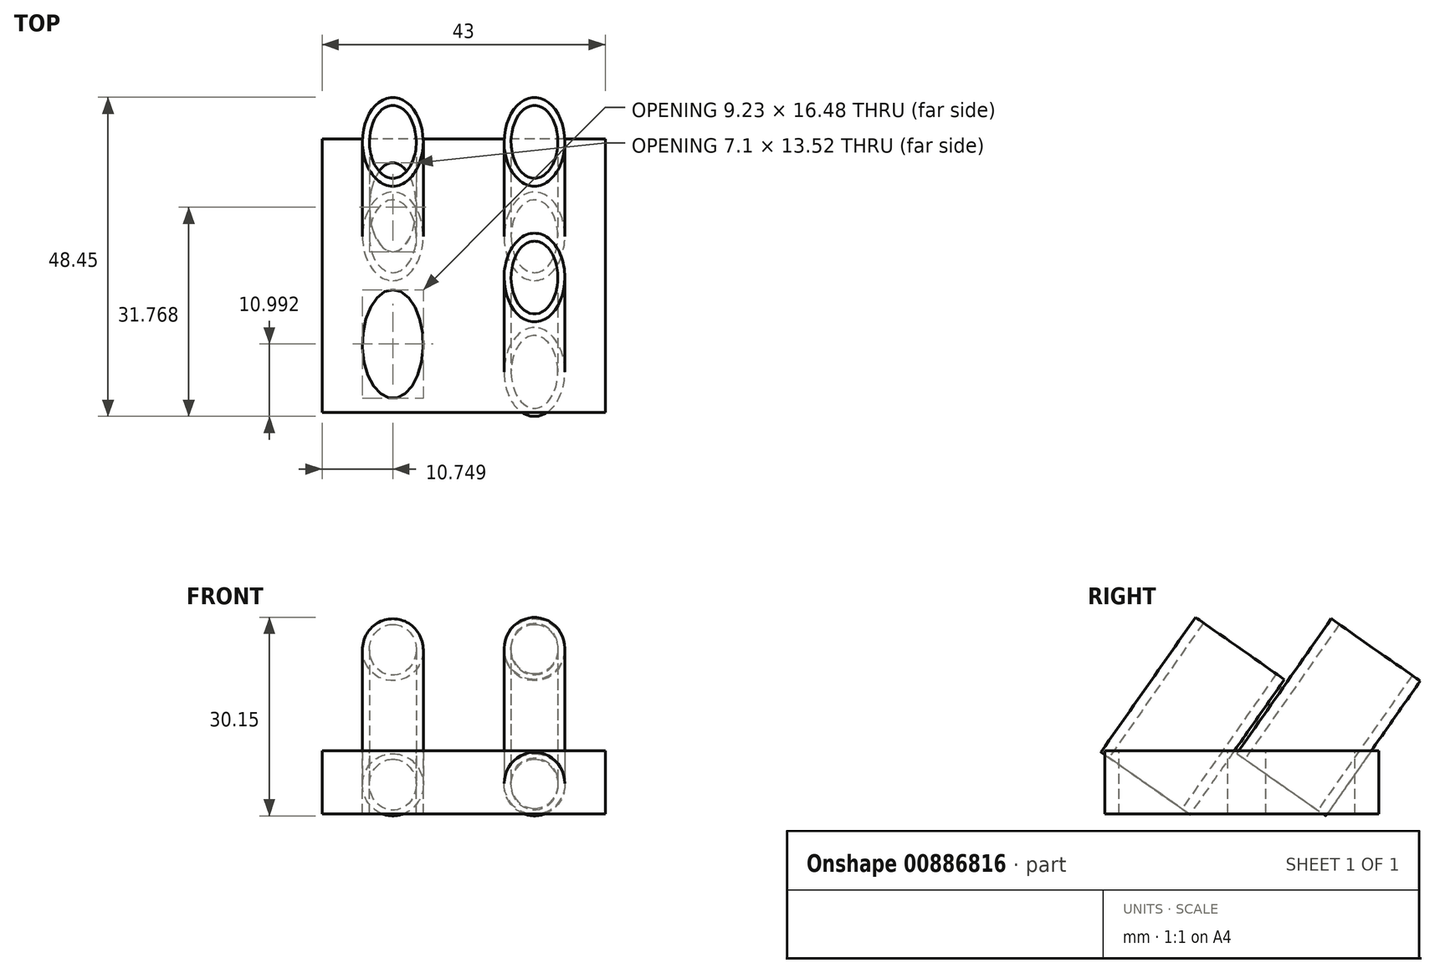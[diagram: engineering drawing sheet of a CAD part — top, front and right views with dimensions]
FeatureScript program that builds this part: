
annotation { "Feature Type Name" : "Feature", "Feature Type Description" : "" }
export const myFeature = defineFeature(function(context is Context, id is Id, definition is map)
    precondition{}
    {
        {
            var Q0;
            Q0=qCreatedBy(makeId("Top.planeOp"),FACE);
            var sketch = newSketch(context, id + "F0", { "sketchPlane" : qUnion([Q0])});
            skLineSegment(sketch, "E0.bottom", {"start": v(21.5, 20.78) * mm, "end": v(-21.5, 20.78) * mm});
            skLineSegment(sketch, "E0.top", {"start": v(21.5, -20.78) * mm, "end": v(-21.5, -20.78) * mm});
            skLineSegment(sketch, "E0.left", {"start": v(21.5, 20.78) * mm, "end": v(21.5, -20.78) * mm});
            skLineSegment(sketch, "E0.right", {"start": v(-21.5, 20.78) * mm, "end": v(-21.5, -20.78) * mm});
            skPoint(sketch, "E0.middle", {"position": v(0, 0) * mm});
            skEllipse(sketch, "E1", {"center": v(-10.75, -10.39) * mm, "majorRadius": 6.76 * mm, "minorRadius": 3.55 * mm, "majorAxis": v(0, 1)});
            skEllipse(sketch, "E2.MirrorC", {"center": v(-10.75, -10.39) * mm, "majorRadius": 6.76 * mm, "minorRadius": 3.55 * mm, "majorAxis": v(0, 1)});
            skEllipse(sketch, "E3.MirrorC", {"center": v(-10.75, -10.39) * mm, "majorRadius": 6.76 * mm, "minorRadius": 3.55 * mm, "majorAxis": v(0, 1)});
            skEllipse(sketch, "E4", {"center": v(-10.75, -10.39) * mm, "majorRadius": 8.24 * mm, "minorRadius": 4.62 * mm, "majorAxis": v(0, 1)});
            skEllipse(sketch, "E5.MirrorC", {"center": v(-10.75, 10.39) * mm, "majorRadius": 8.24 * mm, "minorRadius": 4.62 * mm, "majorAxis": v(0, -1)});
            skEllipse(sketch, "E6.MirrorC", {"center": v(-10.75, 10.39) * mm, "majorRadius": 6.76 * mm, "minorRadius": 3.55 * mm, "majorAxis": v(0, -1)});
            skEllipse(sketch, "E7.MirrorC", {"center": v(-10.75, 10.39) * mm, "majorRadius": 6.76 * mm, "minorRadius": 3.55 * mm, "majorAxis": v(0, -1)});
            skEllipse(sketch, "E8.MirrorC", {"center": v(10.75, -10.39) * mm, "majorRadius": 8.24 * mm, "minorRadius": 4.62 * mm, "majorAxis": v(0, 1)});
            skEllipse(sketch, "E9.MirrorC", {"center": v(10.75, -10.39) * mm, "majorRadius": 6.76 * mm, "minorRadius": 3.55 * mm, "majorAxis": v(0, 1)});
            skEllipse(sketch, "E10.MirrorC", {"center": v(10.75, 10.39) * mm, "majorRadius": 6.76 * mm, "minorRadius": 3.55 * mm, "majorAxis": v(0, -1)});
            skEllipse(sketch, "E11.MirrorC", {"center": v(10.75, 10.39) * mm, "majorRadius": 8.24 * mm, "minorRadius": 4.62 * mm, "majorAxis": v(0, -1)});
            skLineSegment(sketch, "E12", {"start": v(-21.5, 0) * mm, "end": v(21.5, 0) * mm});
            skSolve(sketch);
        }
        {
            var Q0;
            Q0=makeQuery(id+"F0.imprint","IMPRINT",FACE,{"disambiguationData":[TD([[makeQuery(id+"F0.imprint","IMPRINT",EDGE,{"derivedFrom":sQuery(id+"F0.wireOp",EDGE,"E5.MirrorC")}),1.0]])]});
            var Q1;
            Q1=makeQuery(id+"F0.imprint","IMPRINT",FACE,{"disambiguationData":[TD([[makeQuery(id+"F0.imprint","IMPRINT",EDGE,{"derivedFrom":sQuery(id+"F0.wireOp",EDGE,"E10.MirrorC")}),-1.0]])]});
            var Q2;
            Q2=makeQuery(id+"F0.imprint","IMPRINT",FACE,{"disambiguationData":[TD([[makeQuery(id+"F0.imprint","IMPRINT",EDGE,{"derivedFrom":sQuery(id+"F0.wireOp",EDGE,"E8.MirrorC")}),1.0]])]});
            var Q3;
            Q3=makeQuery(id+"F0.imprint","IMPRINT",FACE,{"disambiguationData":[TD([[makeQuery(id+"F0.imprint","IMPRINT",EDGE,{"derivedFrom":sQuery(id+"F0.wireOp",EDGE,"E3.MirrorC")}),-1.0]])]});
            extrude(context, id + "F1", {"entities" : qUnion([Q0, Q1, Q2, Q3]), "depth" : 25 * mm, "offsetDistance" : 25 * mm});
        }
        {
            var Q0;
            Q0=sQuery(id+"F0.wireOp",EDGE,"E12");
            extrude(context, id + "F2", {"bodyType" : ToolBodyType.SURFACE, "surfaceEntities" : qUnion([Q0]), "depth" : 4.4 * mm, "offsetDistance" : 25 * mm});
        }
        {
            var Q0;
            Q0=makeQuery(id+"F1.opExtrude","SWEPT_BODY",BODY,{"disambiguationData":[OSD([sQuery(id+"F0.wireOp",EDGE,"E5.MirrorC"),sQuery(id+"F0.wireOp",EDGE,"E7.MirrorC")])]});
            var Q1;
            Q1=makeQuery(id+"F1.opExtrude","SWEPT_BODY",BODY,{"disambiguationData":[OSD([sQuery(id+"F0.wireOp",EDGE,"E10.MirrorC"),sQuery(id+"F0.wireOp",EDGE,"E11.MirrorC")])]});
            var Q2;
            Q2=makeQuery(id+"F1.opExtrude","SWEPT_BODY",BODY,{"disambiguationData":[OSD([sQuery(id+"F0.wireOp",EDGE,"E3.MirrorC"),sQuery(id+"F0.wireOp",EDGE,"E4")])]});
            var Q3;
            Q3=makeQuery(id+"F1.opExtrude","SWEPT_BODY",BODY,{"disambiguationData":[OSD([sQuery(id+"F0.wireOp",EDGE,"E8.MirrorC"),sQuery(id+"F0.wireOp",EDGE,"E9.MirrorC")])]});
            var Q4;
            Q4=makeQuery(id+"F2.opExtrude","CAP_EDGE",EDGE,{"disambiguationData":[OSD([sQuery(id+"F0.wireOp",EDGE,"E12")])],"isStart":false});
            transform(context, id + "F3", {"entities" : qUnion([Q0, Q1, Q2, Q3]), "transformType" : TransformType.ROTATION, "transformAxis" : qUnion([Q4]), "angle" : 35 * degree, "oppositeDirection" : true, "makeCopy" : false});
        }
        {
            var Q0;
            {var subQ1=sQuery(id+"F0.wireOp",EDGE,"E0.bottom");Q0=makeQuery(id+"F0.imprint","IMPRINT",FACE,{"disambiguationData":[TD([[makeQuery(id+"F0.imprint","IMPRINT",EDGE,{"derivedFrom":subQ1}),1.0]])]});}
            var Q1;
            {var subQ1=sQuery(id+"F0.wireOp",EDGE,"E0.top");Q1=makeQuery(id+"F0.imprint","IMPRINT",FACE,{"disambiguationData":[TD([[makeQuery(id+"F0.imprint","IMPRINT",EDGE,{"derivedFrom":subQ1}),-1.0]])]});}
            var Q2;
            Q2=makeQuery(id+"F0.imprint","IMPRINT",FACE,{"disambiguationData":[TD([[makeQuery(id+"F0.imprint","IMPRINT",EDGE,{"derivedFrom":sQuery(id+"F0.wireOp",EDGE,"E3.MirrorC")}),1.0]])]});
            var Q3;
            Q3=makeQuery(id+"F0.imprint","IMPRINT",FACE,{"disambiguationData":[TD([[makeQuery(id+"F0.imprint","IMPRINT",EDGE,{"derivedFrom":sQuery(id+"F0.wireOp",EDGE,"E3.MirrorC")}),-1.0]])]});
            var Q4;
            Q4=makeQuery(id+"F0.imprint","IMPRINT",FACE,{"disambiguationData":[TD([[makeQuery(id+"F0.imprint","IMPRINT",EDGE,{"derivedFrom":sQuery(id+"F0.wireOp",EDGE,"E7.MirrorC")}),1.0]])]});
            var Q5;
            Q5=makeQuery(id+"F0.imprint","IMPRINT",FACE,{"disambiguationData":[TD([[makeQuery(id+"F0.imprint","IMPRINT",EDGE,{"derivedFrom":sQuery(id+"F0.wireOp",EDGE,"E5.MirrorC")}),1.0]])]});
            var Q6;
            Q6=makeQuery(id+"F0.imprint","IMPRINT",FACE,{"disambiguationData":[TD([[makeQuery(id+"F0.imprint","IMPRINT",EDGE,{"derivedFrom":sQuery(id+"F0.wireOp",EDGE,"E10.MirrorC")}),1.0]])]});
            var Q7;
            Q7=makeQuery(id+"F0.imprint","IMPRINT",FACE,{"disambiguationData":[TD([[makeQuery(id+"F0.imprint","IMPRINT",EDGE,{"derivedFrom":sQuery(id+"F0.wireOp",EDGE,"E10.MirrorC")}),-1.0]])]});
            var Q8;
            Q8=makeQuery(id+"F0.imprint","IMPRINT",FACE,{"disambiguationData":[TD([[makeQuery(id+"F0.imprint","IMPRINT",EDGE,{"derivedFrom":sQuery(id+"F0.wireOp",EDGE,"E8.MirrorC")}),1.0]])]});
            var Q9;
            Q9=makeQuery(id+"F0.imprint","IMPRINT",FACE,{"disambiguationData":[TD([[makeQuery(id+"F0.imprint","IMPRINT",EDGE,{"derivedFrom":sQuery(id+"F0.wireOp",EDGE,"E9.MirrorC")}),1.0]])]});
            extrude(context, id + "F4", {"entities" : qUnion([Q0, Q1, Q2, Q3, Q4, Q5, Q6, Q7, Q8, Q9]), "oppositeDirection" : true, "depth" : 9.6 * mm, "offsetDistance" : 25 * mm});
        }
        {
            var Q0;
            Q0=makeQuery(id+"F1.opExtrude","SWEPT_BODY",BODY,{"disambiguationData":[OSD([sQuery(id+"F0.wireOp",EDGE,"E8.MirrorC"),sQuery(id+"F0.wireOp",EDGE,"E9.MirrorC")])]});
            var Q1;
            Q1=makeQuery(id+"F1.opExtrude","SWEPT_BODY",BODY,{"disambiguationData":[OSD([sQuery(id+"F0.wireOp",EDGE,"E3.MirrorC"),sQuery(id+"F0.wireOp",EDGE,"E4")])]});
            transform(context, id + "F5", {"entities" : qUnion([Q0, Q1]), "transformType" : TransformType.TRANSLATION_3D, "dx" : 0 * mm, "dy" : -3.6 * mm, "dz" : -11.7 * mm, "makeCopy" : false});
        }
        {
            var Q0;
            Q0=makeQuery(id+"F2.opExtrude","SWEPT_BODY",BODY,{"disambiguationData":[OSD([sQuery(id+"F0.wireOp",EDGE,"E12")])]});
            transform(context, id + "F6", {"entities" : qUnion([Q0]), "transformType" : TransformType.TRANSLATION_3D, "dx" : 0 * mm, "dy" : 0 * mm, "dz" : -8 * mm, "makeCopy" : false});
        }
    });
